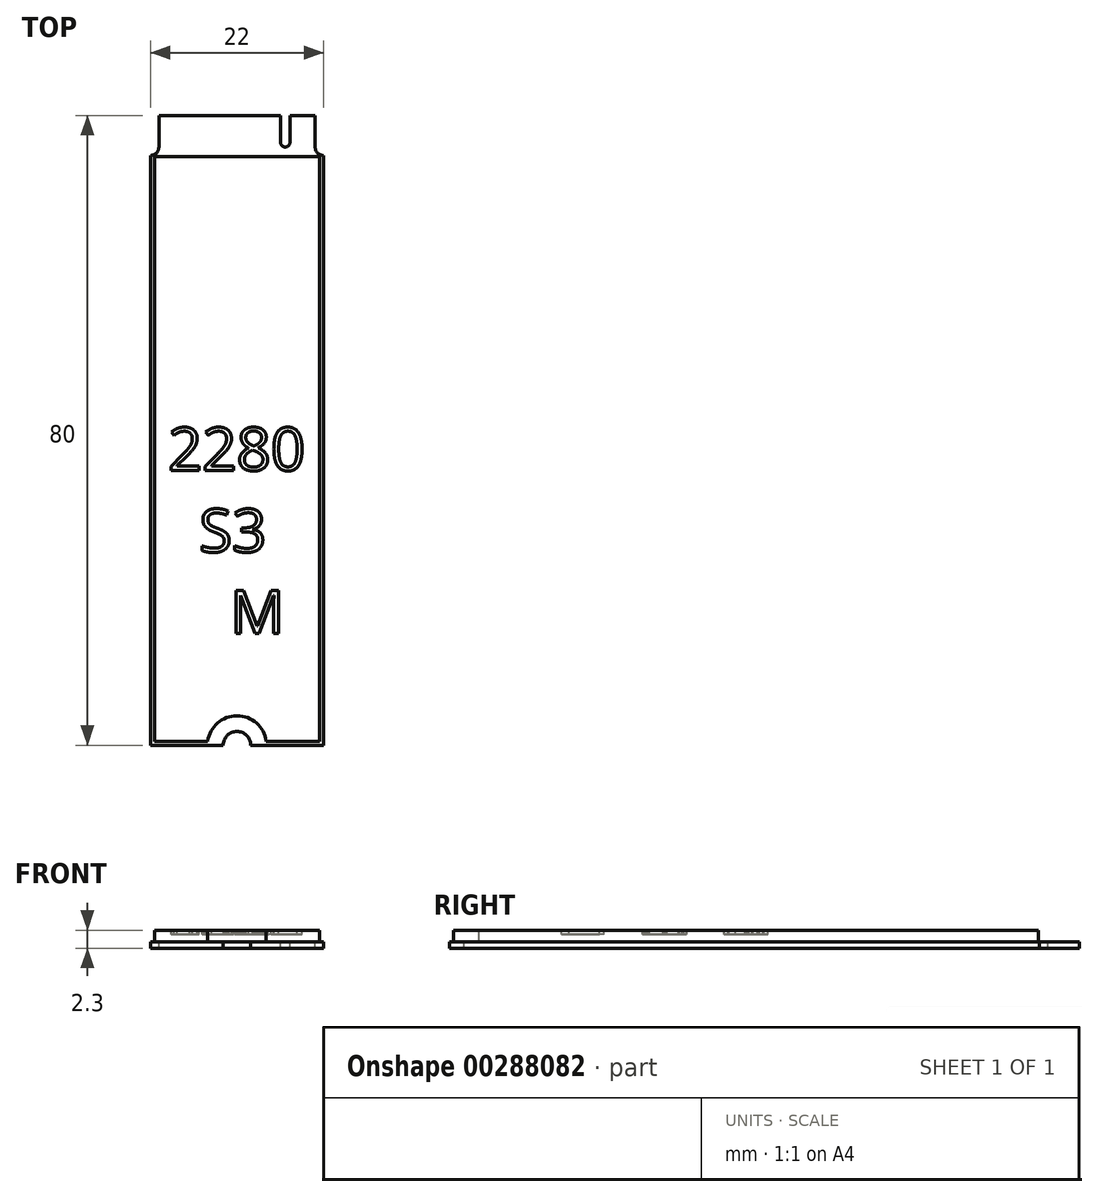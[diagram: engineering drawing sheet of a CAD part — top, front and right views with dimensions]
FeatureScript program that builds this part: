
annotation { "Feature Type Name" : "Feature", "Feature Type Description" : "" }
export const myFeature = defineFeature(function(context is Context, id is Id, definition is map)
    precondition{}
    {
        {
            assignVariable(context, id + "F0", {"name" : "thick", "anyValue" : .8});
        }
        {
            assignVariable(context, id + "F1", {"name" : "compheight", "anyValue" : 1.5});
        }
        {
            var Q0;
            Q0=qCreatedBy(makeId("Top.planeOp"),FACE);
            var sketch = newSketch(context, id + "F2", { "sketchPlane" : qUnion([Q0])});
            skLineSegment(sketch, "E0.bottom", {"start": v(-11, 40) * mm, "end": v(11, 40) * mm});
            skLineSegment(sketch, "E0.top", {"start": v(-11, -40) * mm, "end": v(11, -40) * mm});
            skLineSegment(sketch, "E0.left", {"start": v(-11, 40) * mm, "end": v(-11, -40) * mm});
            skLineSegment(sketch, "E0.right", {"start": v(11, 40) * mm, "end": v(11, -40) * mm});
            skPoint(sketch, "E0.middle", {"position": v(0, 0) * mm});
            skSolve(sketch);
        }
        {
            var Q0;
            Q0=qSketchRegion(id+"F2",true);
            extrude(context, id + "F3", {"entities" : qUnion([Q0]), "depth" : (getVariable(context, 'thick')) * mm});
        }
        {
            var Q0;
            Q0=makeQuery(id+"F3.opExtrude","CAP_FACE",FACE,{"disambiguationData":[OSD([sQuery(id+"F2.wireOp",EDGE,"E0.bottom"),sQuery(id+"F2.wireOp",EDGE,"E0.top"),sQuery(id+"F2.wireOp",EDGE,"E0.left"),sQuery(id+"F2.wireOp",EDGE,"E0.right")])],"isStart":false});
            var sketch = newSketch(context, id + "F4", { "sketchPlane" : qUnion([Q0])});
            skLineSegment(sketch, "E1.bottom", {"start": v(-10.5, -39.5) * mm, "end": v(10.5, -39.5) * mm});
            skLineSegment(sketch, "E1.top", {"start": v(-10.5, 34.8) * mm, "end": v(10.5, 34.8) * mm});
            skLineSegment(sketch, "E1.left", {"start": v(-10.5, -39.5) * mm, "end": v(-10.5, 34.8) * mm});
            skLineSegment(sketch, "E1.right", {"start": v(10.5, -39.5) * mm, "end": v(10.5, 34.8) * mm});
            skLineSegment(sketch, "E2", {"start": v(0, -40) * mm, "end": v(0, -39.5) * mm, "construction": true});
            skLineSegment(sketch, "E3", {"start": v(10.5, -2.35) * mm, "end": v(11, -2.35) * mm, "construction": true});
            skLineSegment(sketch, "E4", {"start": v(0, 34.8) * mm, "end": v(0, 40) * mm, "construction": true});
            skSolve(sketch);
        }
        {
            var Q0;
            Q0=qSketchRegion(id+"F4",true);
            extrude(context, id + "F5", {"entities" : qUnion([Q0]), "operationType" : NewBodyOperationType.ADD, "depth" : (getVariable(context, 'compheight')) * mm});
        }
        {
            var Q0;
            Q0=makeQuery(id+"F3.opExtrude","CAP_FACE",FACE,{"disambiguationData":[OSD([sQuery(id+"F2.wireOp",EDGE,"E0.bottom"),sQuery(id+"F2.wireOp",EDGE,"E0.top"),sQuery(id+"F2.wireOp",EDGE,"E0.left"),sQuery(id+"F2.wireOp",EDGE,"E0.right")])],"isStart":false});
            var sketch = newSketch(context, id + "F6", { "sketchPlane" : qUnion([Q0])});
            skLineSegment(sketch, "E5", {"start": v(0, 40) * mm, "end": v(0, 34.8) * mm, "construction": true});
            skLineSegment(sketch, "E6", {"start": v(-9.92, 40) * mm, "end": v(-9.92, 36) * mm});
            skArc(sketch, "E7", {"start": v(-11, 34.93) * mm, "mid": v(-10.24, 35.24) * mm, "end": v(-9.92, 36) * mm});
            skLineSegment(sketch, "E8", {"start": v(-9.92, 40) * mm, "end": v(-11, 40) * mm});
            skLineSegment(sketch, "E9", {"start": v(-11, 40) * mm, "end": v(-11, 34.93) * mm});
            skLineSegment(sketch, "E10.MirrorCS", {"start": v(9.93, 40) * mm, "end": v(9.93, 36) * mm});
            skLineSegment(sketch, "E11.MirrorCS", {"start": v(9.92, 40) * mm, "end": v(11, 40) * mm});
            skLineSegment(sketch, "E12.MirrorCS", {"start": v(11, 40) * mm, "end": v(11, 34.93) * mm});
            skArc(sketch, "E13.MirrorCS", {"start": v(11, 34.93) * mm, "mid": v(10.24, 35.24) * mm, "end": v(9.92, 36) * mm});
            skLineSegment(sketch, "E14", {"start": v(-9.92, 40) * mm, "end": v(9.92, 40) * mm, "construction": true});
            skLineSegment(sketch, "E15", {"start": v(0, 40) * mm, "end": v(6.13, 40) * mm, "construction": true});
            skLineSegment(sketch, "E16", {"start": v(6.13, 40) * mm, "end": v(6.13, 36.6) * mm, "construction": true});
            skLineSegment(sketch, "E17", {"start": v(0, 40) * mm, "end": v(-5.63, 40) * mm, "construction": true});
            skLineSegment(sketch, "E18", {"start": v(-9.92, 36) * mm, "end": v(6.13, 36) * mm, "construction": true});
            skArc(sketch, "E19", {"start": v(5.53, 36.6) * mm, "mid": v(6.13, 36) * mm, "end": v(6.73, 36.6) * mm});
            skLineSegment(sketch, "E20", {"start": v(6.13, 36.6) * mm, "end": v(5.53, 36.6) * mm, "construction": true});
            skLineSegment(sketch, "E21", {"start": v(6.73, 36.6) * mm, "end": v(6.73, 40) * mm});
            skLineSegment(sketch, "E22", {"start": v(6.73, 40) * mm, "end": v(5.53, 40) * mm});
            skLineSegment(sketch, "E23", {"start": v(5.53, 40) * mm, "end": v(5.53, 36.6) * mm});
            skLineSegment(sketch, "E24", {"start": v(-6.23, 40) * mm, "end": v(-6.23, 26.62) * mm, "construction": true});
            skLineSegment(sketch, "E25", {"start": v(-5.03, 40) * mm, "end": v(-5.03, 26.62) * mm, "construction": true});
            skArc(sketch, "E26", {"start": v(-6.23, 26.62) * mm, "mid": v(-5.63, 26.02) * mm, "end": v(-5.03, 26.62) * mm, "construction": true});
            skLineSegment(sketch, "E27", {"start": v(-6.23, 26.62) * mm, "end": v(-5.03, 26.62) * mm, "construction": true});
            skLineSegment(sketch, "E28", {"start": v(-5.63, 40) * mm, "end": v(-5.63, 26.62) * mm, "construction": true});
            skLineSegment(sketch, "E29", {"start": v(-6.23, 40) * mm, "end": v(-5.03, 40) * mm});
            skSolve(sketch);
        }
        {
            var Q0;
            Q0=qSketchRegion(id+"F6",true);
            extrude(context, id + "F7", {"entities" : qUnion([Q0]), "operationType" : NewBodyOperationType.REMOVE, "endBound" : BoundingType.THROUGH_ALL, "oppositeDirection" : true, "depth" : 25 * mm});
        }
        {
            var Q0;
            Q0=makeQuery(id+"F3.opExtrude","CAP_FACE",FACE,{"disambiguationData":[OSD([sQuery(id+"F2.wireOp",EDGE,"E0.bottom"),sQuery(id+"F2.wireOp",EDGE,"E0.top"),sQuery(id+"F2.wireOp",EDGE,"E0.left"),sQuery(id+"F2.wireOp",EDGE,"E0.right")])],"isStart":true});
            var sketch = newSketch(context, id + "F8", { "sketchPlane" : qUnion([Q0])});
            skCircle(sketch, "E30", {"center": v(0, 40) * mm, "radius": 1.75 * mm});
            skSolve(sketch);
        }
        {
            var Q0;
            Q0=qSketchRegion(id+"F8",true);
            extrude(context, id + "F9", {"entities" : qUnion([Q0]), "operationType" : NewBodyOperationType.REMOVE, "endBound" : BoundingType.THROUGH_ALL, "oppositeDirection" : true, "depth" : 25 * mm});
        }
        {
            var Q0;
            Q0=makeQuery(id+"F5.opExtrude","CAP_FACE",FACE,{"disambiguationData":[OSD([sQuery(id+"F4.wireOp",EDGE,"E1.bottom"),sQuery(id+"F4.wireOp",EDGE,"E1.top"),sQuery(id+"F4.wireOp",EDGE,"E1.left"),sQuery(id+"F4.wireOp",EDGE,"E1.right")])],"isStart":false});
            var sketch = newSketch(context, id + "F10", { "sketchPlane" : qUnion([Q0])});
            skArc(sketch, "E31.0", {"start": v(1.68, -39.5) * mm, "mid": v(0, -38.25) * mm, "end": v(-1.68, -39.5) * mm});
            skArc(sketch, "E32.0", {"start": v(3.72, -39.5) * mm, "mid": v(0, -36.25) * mm, "end": v(-3.72, -39.5) * mm});
            skLineSegment(sketch, "E33", {"start": v(-1.68, -39.5) * mm, "end": v(-3.72, -39.5) * mm});
            skLineSegment(sketch, "E34", {"start": v(1.68, -39.5) * mm, "end": v(3.72, -39.5) * mm});
            skSolve(sketch);
        }
        {
            var Q0;
            Q0=qSketchRegion(id+"F10",true);
            var Q1;
            Q1=makeQuery(id+"F3.opExtrude","CAP_FACE",FACE,{"disambiguationData":[OSD([sQuery(id+"F2.wireOp",EDGE,"E0.bottom"),sQuery(id+"F2.wireOp",EDGE,"E0.top"),sQuery(id+"F2.wireOp",EDGE,"E0.left"),sQuery(id+"F2.wireOp",EDGE,"E0.right")])],"isStart":false});
            extrude(context, id + "F11", {"entities" : qUnion([Q0]), "operationType" : NewBodyOperationType.REMOVE, "endBound" : BoundingType.UP_TO_SURFACE, "oppositeDirection" : true, "endBoundEntityFace" : qUnion([Q1]), "depth" : 25 * mm});
        }
        {
            var Q0;
            Q0=makeQuery(id+"F5.opExtrude","CAP_FACE",FACE,{"disambiguationData":[OSD([sQuery(id+"F4.wireOp",EDGE,"E1.bottom"),sQuery(id+"F4.wireOp",EDGE,"E1.top"),sQuery(id+"F4.wireOp",EDGE,"E1.left"),sQuery(id+"F4.wireOp",EDGE,"E1.right")])],"isStart":false});
            var sketch = newSketch(context, id + "F12", { "sketchPlane" : qUnion([Q0])});
            skLineSegment(sketch, "E35", {"start": v(10.5, -39.5) * mm, "end": v(-10.5, 34.8) * mm, "construction": true});
            skText(sketch, "E36", { "text": "2280\n  S3\n    M", "fontName": "OpenSans-Regular.ttf"});
            skPoint(sketch, "E37", {"position": v(0, -2.35) * mm});
            const initialGuessF12  = {"E36": [-0.00876, -0.00509, 1, 0, 0.00548]};
            skSetInitialGuess(sketch, initialGuessF12);
            skSolve(sketch);
        }
        {
            var Q0;
            Q0=qSketchRegion(id+"F12",true);
            extrude(context, id + "F13", {"entities" : qUnion([Q0]), "operationType" : NewBodyOperationType.REMOVE, "oppositeDirection" : true, "depth" : .5 * mm});
        }
    });
